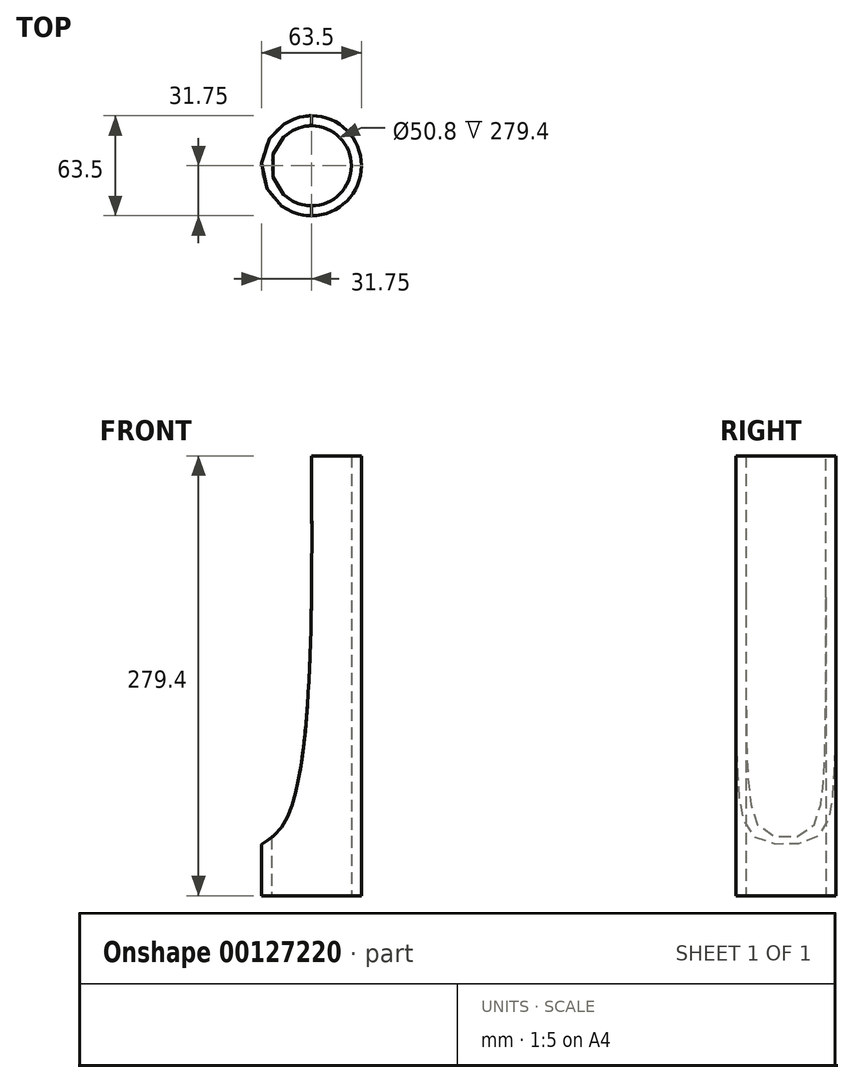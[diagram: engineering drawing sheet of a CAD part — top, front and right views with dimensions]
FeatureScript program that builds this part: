
annotation { "Feature Type Name" : "Feature", "Feature Type Description" : "" }
export const myFeature = defineFeature(function(context is Context, id is Id, definition is map)
    precondition{}
    {
        {
            var Q0;
            Q0=qCreatedBy(makeId("Top.planeOp"),FACE);
            var sketch = newSketch(context, id + "F0", { "sketchPlane" : qUnion([Q0])});
            skCircle(sketch, "E0", {"center": v(0, 0) * mm, "radius": 25.4 * mm});
            skCircle(sketch, "E1.0", {"center": v(0, 0) * mm, "radius": 31.75 * mm});
            skSolve(sketch);
        }
        {
            var Q0;
            Q0=makeQuery(id+"F0.imprint","IMPRINT",FACE,{"disambiguationData":[TD([[makeQuery(id+"F0.imprint","IMPRINT",EDGE,{"derivedFrom":sQuery(id+"F0.wireOp",EDGE,"E0")}),-1.0]])]});
            extrude(context, id + "F1", {"entities" : qUnion([Q0]), "depth" : 279.4 * mm});
        }
        {
            var Q0;
            Q0=qCreatedBy(makeId("Front.planeOp"),FACE);
            var sketch = newSketch(context, id + "F2", { "sketchPlane" : qUnion([Q0])});
            skFitSpline(sketch, "E2", {"points": [v(0, 298.3) * mm, v(-16.88, 46.9) * mm, v(-57.35, 12.28) * mm], "startDerivative": vector(0, -370.25) * mm, "endDerivative": vector(-159.43, -197.85) * mm});
            skLineSegment(sketch, "E3", {"start": v(-57.35, 12.28) * mm, "end": v(-57.35, 299.44) * mm});
            skLineSegment(sketch, "E4", {"start": v(-57.35, 299.44) * mm, "end": v(0, 298.3) * mm});
            skSolve(sketch);
        }
        {
            var Q0;
            Q0 = qSketchRegion(id + "F2", true);
            extrude(context, id + "F3", {"entities" : qUnion([Q0]), "operationType" : NewBodyOperationType.REMOVE, "endBound" : BoundingType.THROUGH_ALL, "depth" : 25.4 * mm, "hasSecondDirection" : true, "secondDirectionBound" : SecondDirectionBoundingType.THROUGH_ALL, "secondDirectionOppositeDirection" : true, "secondDirectionDepth" : 25.4 * mm});
        }
    });
